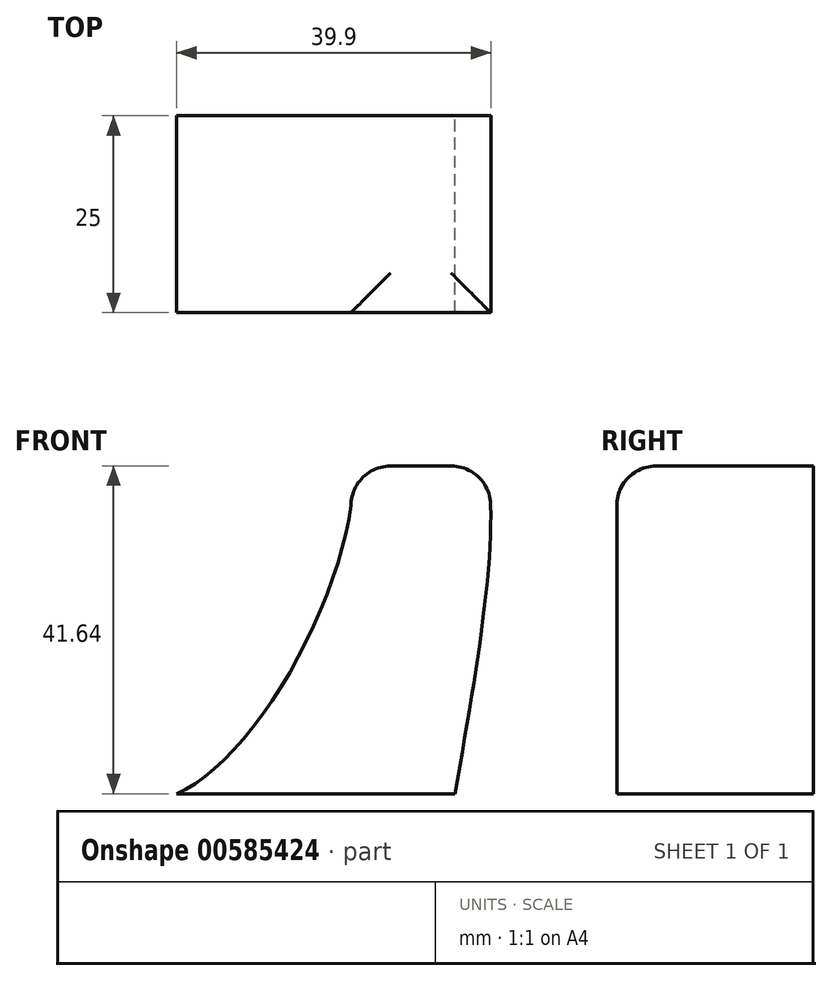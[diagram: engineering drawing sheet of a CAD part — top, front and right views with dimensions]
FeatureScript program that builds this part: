
annotation { "Feature Type Name" : "Feature", "Feature Type Description" : "" }
export const myFeature = defineFeature(function(context is Context, id is Id, definition is map)
    precondition{}
    {
        {
            var Q0;
            Q0=qCreatedBy(makeId("Front.planeOp"),FACE);
            var sketch = newSketch(context, id + "F0", { "sketchPlane" : qUnion([Q0])});
            skLineSegment(sketch, "E0", {"start": v(0, 0) * mm, "end": v(40.4, 0) * mm});
            skFitSpline(sketch, "E1", {"points": [v(40.4, 0) * mm, v(40.4, 47.93) * mm, v(8.83, 26.85) * mm, v(0, 0) * mm], "startDerivative": vector(31.46, 178.87) * mm, "endDerivative": vector(-9.32, -89.27) * mm});
            skSolve(sketch);
        }
        {
            var Q0;
            Q0 = qSketchRegion(id + "F0", true);
            extrude(context, id + "F1", {"entities" : qUnion([Q0]), "depth" : 25 * mm, "offsetDistance" : 25 * mm});
        }
        {
            var Q0;
            Q0=qCreatedBy(makeId("Front.planeOp"),FACE);
            var sketch = newSketch(context, id + "F2", { "sketchPlane" : qUnion([Q0])});
            skFitSpline(sketch, "E2", {"points": [v(0, 0) * mm, v(18.04, 13.13) * mm, v(25.44, 45.03) * mm, v(1.95, 29.94) * mm, v(0, 0) * mm]});
            skSolve(sketch);
        }
        {
            var Q0;
            Q0=makeQuery(id+"F2.imprint","IMPRINT",FACE,{"disambiguationData":[TD([[makeQuery(id+"F2.imprint","IMPRINT",EDGE,{"derivedFrom":sQuery(id+"F2.wireOp",EDGE,"E2")}),1.0]])]});
            extrude(context, id + "F3", {"entities" : qUnion([Q0]), "operationType" : NewBodyOperationType.REMOVE, "depth" : 52.7 * mm, "offsetDistance" : 25 * mm});
        }
        {
            var Q0;
            Q0=qCreatedBy(makeId("Front.planeOp"),FACE);
            var sketch = newSketch(context, id + "F4", { "sketchPlane" : qUnion([Q0])});
            skLineSegment(sketch, "E3.bottom", {"start": v(25.96, 41.64) * mm, "end": v(47.8, 41.64) * mm});
            skLineSegment(sketch, "E3.top", {"start": v(25.96, 49.14) * mm, "end": v(47.8, 49.14) * mm});
            skLineSegment(sketch, "E3.left", {"start": v(25.96, 41.64) * mm, "end": v(25.96, 49.14) * mm});
            skLineSegment(sketch, "E3.right", {"start": v(47.8, 41.64) * mm, "end": v(47.8, 49.14) * mm});
            skSolve(sketch);
        }
        {
            var Q0;
            Q0 = qSketchRegion(id + "F4", true);
            extrude(context, id + "F5", {"entities" : qUnion([Q0]), "operationType" : NewBodyOperationType.REMOVE, "depth" : 59 * mm, "offsetDistance" : 25 * mm});
        }
        {
            var Q0;
            Q0=makeQuery(id+"F5.boolean.opBoolean","INTERSECT",EDGE,{"derivedFrom":[makeQuery(id+"F3.boolean.opBoolean","COPY",FACE,{"derivedFrom":makeQuery(id+"F3.opExtrude","SWEPT_FACE",FACE,{"disambiguationData":[OSD([sQuery(id+"F2.wireOp",EDGE,"E2")])]})}),makeQuery(id+"F5.opExtrude","SWEPT_FACE",FACE,{"disambiguationData":[OSD([sQuery(id+"F4.wireOp",EDGE,"E3.bottom")])]})]});
            var Q1;
            Q1=makeQuery(id+"F5.boolean.opBoolean","INTERSECT",EDGE,{"derivedFrom":[makeQuery(id+"F1.opExtrude","CAP_FACE",FACE,{"disambiguationData":[OSD([sQuery(id+"F0.wireOp",EDGE,"E0"),sQuery(id+"F0.wireOp",EDGE,"E1")])],"isStart":false}),makeQuery(id+"F5.opExtrude","SWEPT_FACE",FACE,{"disambiguationData":[OSD([sQuery(id+"F4.wireOp",EDGE,"E3.bottom")])]})]});
            var Q2;
            Q2=makeQuery(id+"F5.boolean.opBoolean","COPY",EDGE,{"derivedFrom":makeQuery(id+"F5.opExtrude","CAP_EDGE",EDGE,{"disambiguationData":[OSD([sQuery(id+"F4.wireOp",EDGE,"E3.bottom")])],"isStart":true})});
            var Q3;
            Q3=makeQuery(id+"F5.boolean.opBoolean","INTERSECT",EDGE,{"derivedFrom":[makeQuery(id+"F1.opExtrude","SWEPT_FACE",FACE,{"disambiguationData":[OSD([sQuery(id+"F0.wireOp",EDGE,"E1")])]}),makeQuery(id+"F5.opExtrude","SWEPT_FACE",FACE,{"disambiguationData":[OSD([sQuery(id+"F4.wireOp",EDGE,"E3.bottom")])]})]});
            fillet(context, id + "F6", {"entities" : qUnion([Q0, Q1, Q2, Q3]), "radius" : 5 * mm, "tangentPropagation" : true, "allowEdgeOverflow" : false});
        }
    });
